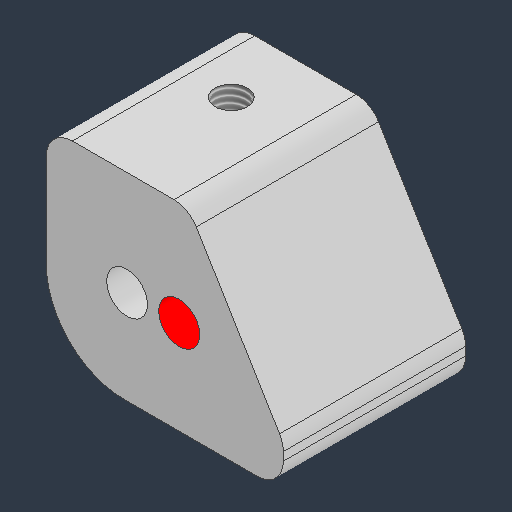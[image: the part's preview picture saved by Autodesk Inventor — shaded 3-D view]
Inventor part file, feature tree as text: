
AUTODESK INVENTOR PART (.ipt)
format: ipt  version: 2024.3 (Build 283343000, 343)  size: 163,840 bytes
history: native  units: in
note: dims shown in document units (in); Inventor stores cm internally (conversion verified against a paired STEP export)
features: other x3, sketch x3, hole x3, fillet x2, extrude x1
ambient origin geometry x8: Origin, YZ Plane, XZ Plane, XY Plane, X Axis, Y Axis, Z Axis, Center Point
bodies: Solid1 (feature_tree), Solid1_1 (feature_tree)
feature tree (12):
  other  "BEARING,MOUNT,SIDE,ELEVATOR.ipt"
  extrude  "Extrusion1"  Depth=0.95in
  sketch  "Sketch2"  dims[d2=0.1875in d3=0.875in d4=0.0in]
  hole  "Hole1"  [1 undecoded]
  hole  "Hole2"  [1 undecoded]
  hole  "Hole3"  [1 undecoded]
  fillet  "Fillet1"  Radius=0.375in
  fillet  "Fillet2"  Radius=0.125in
  sketch  "Sketch1"  dims[d0=0.825in d1=0.95in]
  sketch  "Sketch3"  dims[d5=0.197in d6=0.75in d7=0.217in d8=0.077in d9=90.0deg d10=1.0in d11=0.8108in d12=0.196in d13=0.75in d14=0.385in d15=0.25in d16=0.5635in d17=1.0in d18=0.8108in d19=0.3125in d21=0.3125in d22=0.156in d23=0.38in d24=0.375in d25=0.25in d26=0.5635in d27=0.536in d28=0.8108in d29=0.375in d30=0.125in d31=0.325in d32=0.3937in]
  other  "Solid1::BEARING,MOUNT,SIDE,ELEVATOR.ipt"
  other  "TaggingFeature1"
note: 3 required parameter values undecoded (feature->parameter linkage not recoverable at this tier; creation-order binding heuristic only, values carry confidence <= 0.55)
